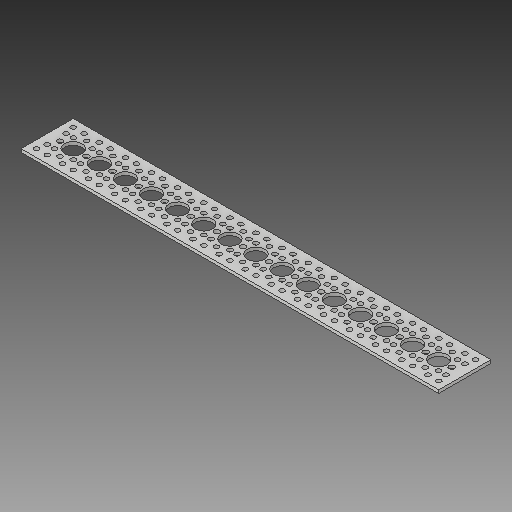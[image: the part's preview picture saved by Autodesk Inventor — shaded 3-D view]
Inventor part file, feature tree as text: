
AUTODESK INVENTOR PART (.ipt)
format: ipt  version: 2017 (Build 210142000, 142)  size: 311,808 bytes
history: native  units: in
note: dims shown in document units (in); Inventor stores cm internally (conversion verified against a paired STEP export)
features: mirror x1
ambient origin geometry x8: Origin, YZ Plane, XZ Plane, XY Plane, X Axis, Y Axis, Z Axis, Center Point
bodies: Solid1 (feature_tree)
feature tree (1):
  mirror  "Mirror1"
